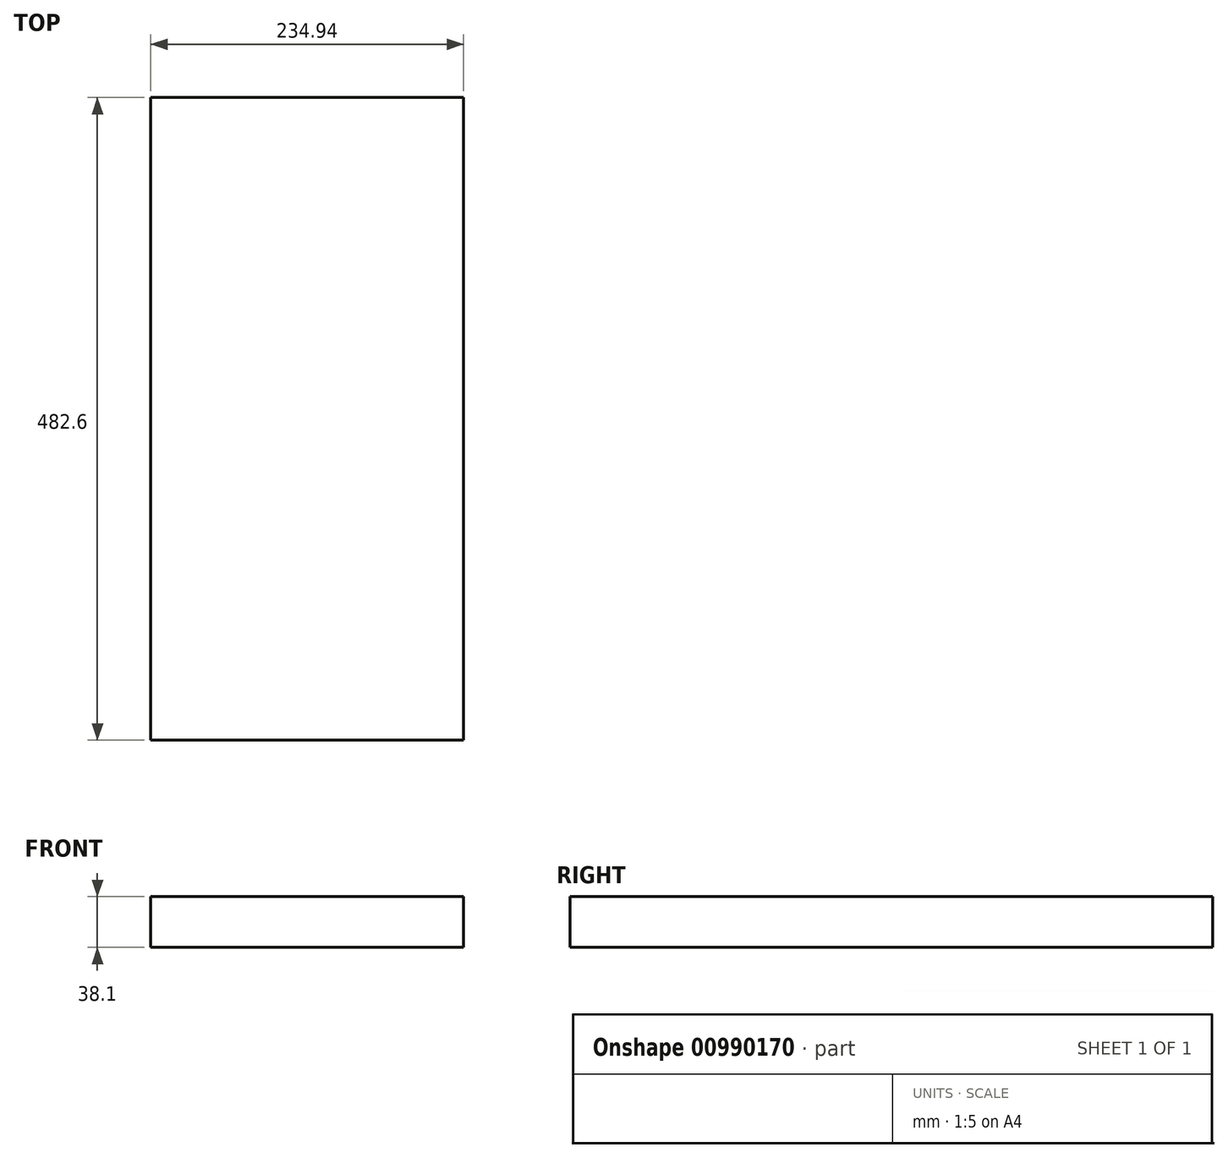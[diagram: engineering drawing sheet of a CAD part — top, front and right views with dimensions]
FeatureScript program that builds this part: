
annotation { "Feature Type Name" : "Feature", "Feature Type Description" : "" }
export const myFeature = defineFeature(function(context is Context, id is Id, definition is map)
    precondition{}
    {
        {
            assignVariable(context, id + "F0", {"name" : "w", "anyValue" : 38.1 * mm});
        }
        {
            var Q0;
            Q0=qCreatedBy(makeId("Top.planeOp"),FACE);
            var sketch = newSketch(context, id + "F1", { "sketchPlane" : qUnion([Q0])});
            skLineSegment(sketch, "E0.bottom", {"start": v(117.48, 241.3) * mm, "end": v(-117.47, 241.3) * mm});
            skLineSegment(sketch, "E0.top", {"start": v(117.48, -241.3) * mm, "end": v(-117.47, -241.3) * mm});
            skLineSegment(sketch, "E0.left", {"start": v(117.48, 241.3) * mm, "end": v(117.48, -241.3) * mm});
            skLineSegment(sketch, "E0.right", {"start": v(-117.47, 241.3) * mm, "end": v(-117.47, -241.3) * mm});
            skPoint(sketch, "E0.middle", {"position": v(0, 0) * mm});
            skSolve(sketch);
        }
        {
            var Q0;
            Q0=qSketchRegion(id+"F1",true);
            extrude(context, id + "F2", {"entities" : qUnion([Q0]), "depth" : getVariable(context, 'w'), "offsetDistance" : 25.4 * mm});
        }
    });
